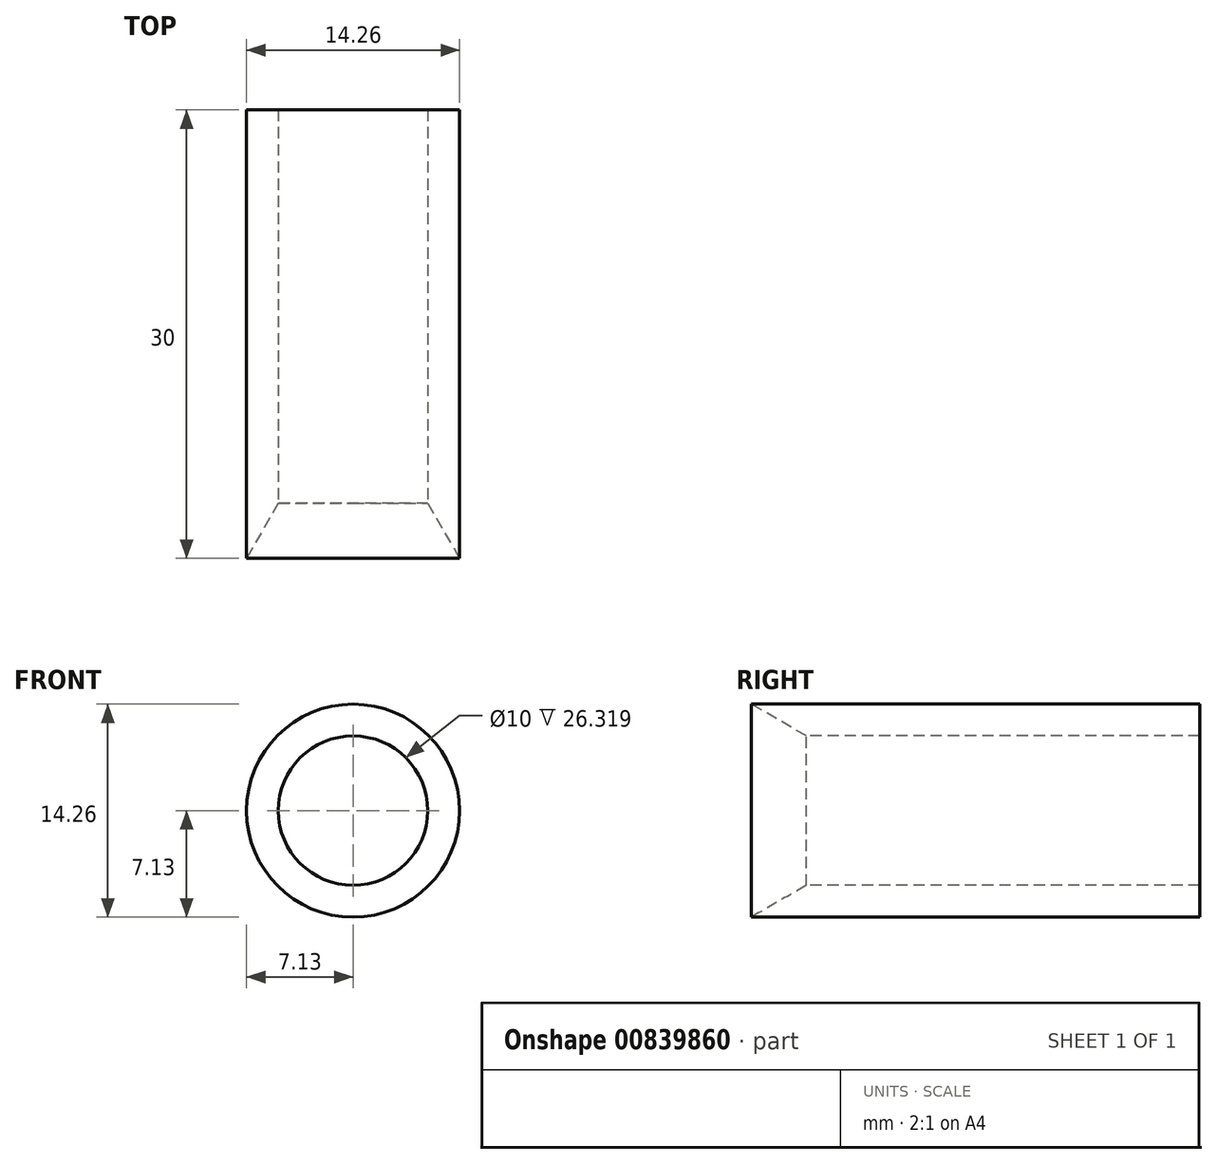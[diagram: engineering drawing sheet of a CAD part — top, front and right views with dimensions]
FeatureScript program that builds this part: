
annotation { "Feature Type Name" : "Feature", "Feature Type Description" : "" }
export const myFeature = defineFeature(function(context is Context, id is Id, definition is map)
    precondition{}
    {
        {
            var Q0;
            Q0=qCreatedBy(makeId("Top.planeOp"),FACE);
            var sketch = newSketch(context, id + "F0", { "sketchPlane" : qUnion([Q0])});
            skLineSegment(sketch, "E0", {"start": v(-7.13, 13.92) * mm, "end": v(-7.12, -16.08) * mm});
            skLineSegment(sketch, "E1", {"start": v(-7.12, -16.08) * mm, "end": v(-5, -12.4) * mm});
            skLineSegment(sketch, "E2", {"start": v(-5, -12.4) * mm, "end": v(-5, 13.92) * mm});
            skLineSegment(sketch, "E3", {"start": v(-5, 13.92) * mm, "end": v(-7.12, 13.92) * mm});
            skLineSegment(sketch, "E4", {"start": v(0, -15.7) * mm, "end": v(0, 16.44) * mm, "construction": true});
            skSolve(sketch);
        }
        {
            var Q0;
            Q0 = qSketchRegion(id + "F0", true);
            var Q1;
            Q1=sQuery(id+"F0.wireOp",EDGE,"E4");
            revolve(context, id + "F1", {"surfaceOperationType" : NewSurfaceOperationType.NEW, "entities" : qUnion([Q0]), "axis" : qUnion([Q1]), "revolveType" : RevolveType.FULL});
        }
    });
